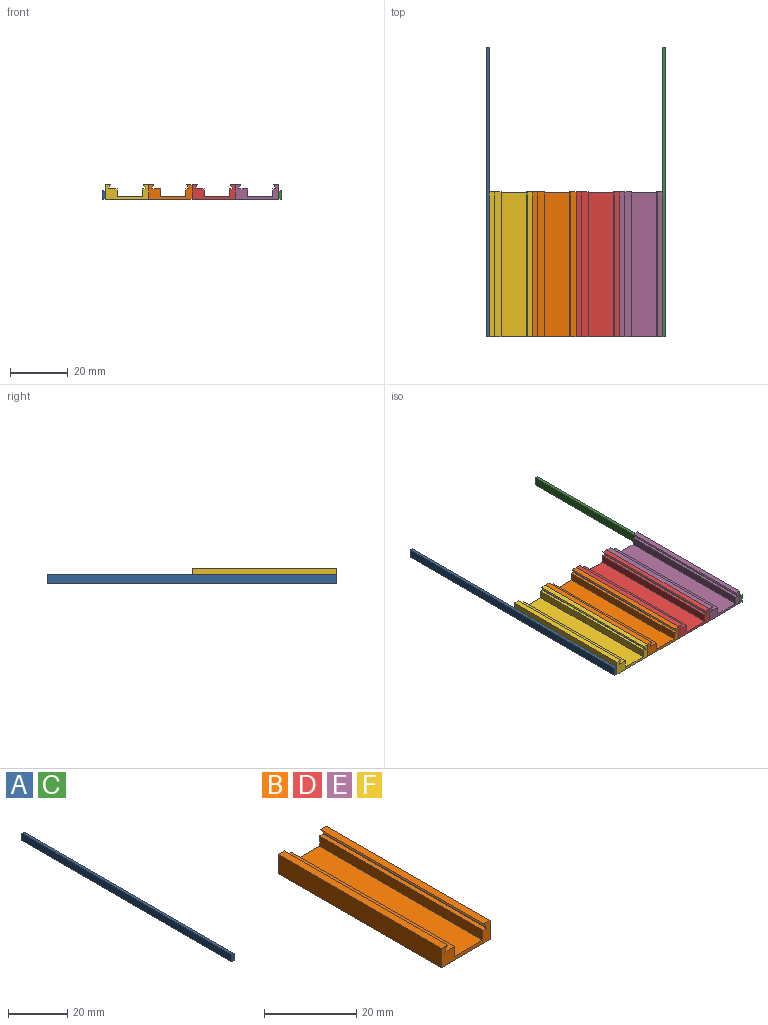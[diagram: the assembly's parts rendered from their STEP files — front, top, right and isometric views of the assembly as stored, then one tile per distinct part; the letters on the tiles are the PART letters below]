
ASSEMBLY  parts=6 mates=5
PART A: 6 faces, bbox 1x100x3 mm
  f0: plane 100x3mm, normal (-1,0,0), area 300mm2, adj f1,f3,f4,f5
  f1: plane 100x1mm, normal (0,0,-1), area 100mm2, adj f0,f2,f4,f5
  f2: plane 100x3mm, normal (1,0,0), area 300mm2, adj f1,f3,f4,f5
  f3: plane 100x1mm, normal (0,0,1), area 100mm2, adj f0,f2,f4,f5
  f4: plane 3x1mm, normal (0,-1,0), area 3mm2, adj f0,f1,f2,f3
  f5: plane 3x1mm, normal (0,1,0), area 3mm2, adj f0,f1,f2,f3
PART B: 16 faces, bbox 15x50x5.1 mm
  f0: plane 50x1.84mm, normal (0,0,1), area 92.1mm2, adj f1,f13,f14,f15
  f1: plane 50x5.1mm, normal (-1,0,0), area 255mm2, adj f0,f2,f14,f15
  f2: plane 50x15mm, normal (0,0,-1), area 750mm2, adj f1,f3,f14,f15
  f3: plane 50x5.1mm, normal (1,0,0), area 255mm2, adj f2,f4,f14,f15
  f4: plane 50x1.84mm, normal (0,0,1), area 92.1mm2, adj f3,f5,f14,f15
  f5: plane 50x1.2mm, normal (-0.87,0,-0.5), area 69.3mm2, adj f4,f6,f14,f15
  f6: plane 50x0.3mm, normal (-1,0,0), area 15mm2, adj f5,f7,f14,f15
  f7: plane 50x1mm, normal (0,0,1), area 50mm2, adj f6,f8,f14,f15
  f8: plane 50x2.7mm, normal (-1,0,0), area 135mm2, adj f7,f9,f14,f15
  f9: plane 50x8.7mm, normal (0,0,1), area 435mm2, adj f8,f10,f14,f15
  f10: plane 50x2.7mm, normal (1,0,0), area 135mm2, adj f9,f11,f14,f15
  f11: plane 50x3mm, normal (0,0,1), area 150mm2, adj f10,f12,f14,f15
  f12: plane 50x0.3mm, normal (1,0,0), area 15mm2, adj f11,f13,f14,f15
  f13: plane 50x1.2mm, normal (0.87,0,-0.5), area 69.3mm2, adj f0,f12,f14,f15
  f14: plane 15x5.1mm, normal (0,-1,0), area 34.8mm2, adj f0,f1,f2,f3,f4,f5,f6,f7
  f15: plane 15x5.1mm, normal (0,1,0), area 34.8mm2, adj f0,f1,f2,f3,f4,f5,f6,f7
PART C: same geometry as A
PART D: same geometry as B
PART E: same geometry as B
PART F: same geometry as B
PLACE A t=(-45,50,0)mm
PLACE B t=(-29,0,0)mm
PLACE C t=(16,50,0)mm
PLACE D t=(-14,0,0)mm
PLACE E t=(1,0,0)mm
PLACE F t=(-44,0,0)mm
MATE fastened E.f3 <-> C.f0  axis (1,0,0) through (16,-50,0)mm
MATE fastened A.f2 <-> F.f1  axis (1,0,0) through (-44,-50,0)mm
MATE fastened D.f1 <-> B.f3  axis (-1,0,0) through (-14,-50,0)mm
MATE fastened F.f3 <-> B.f1  axis (1,0,0) through (-29,-50,0)mm
MATE fastened D.f3 <-> E.f1  axis (1,0,0) through (1,-50,0)mm
